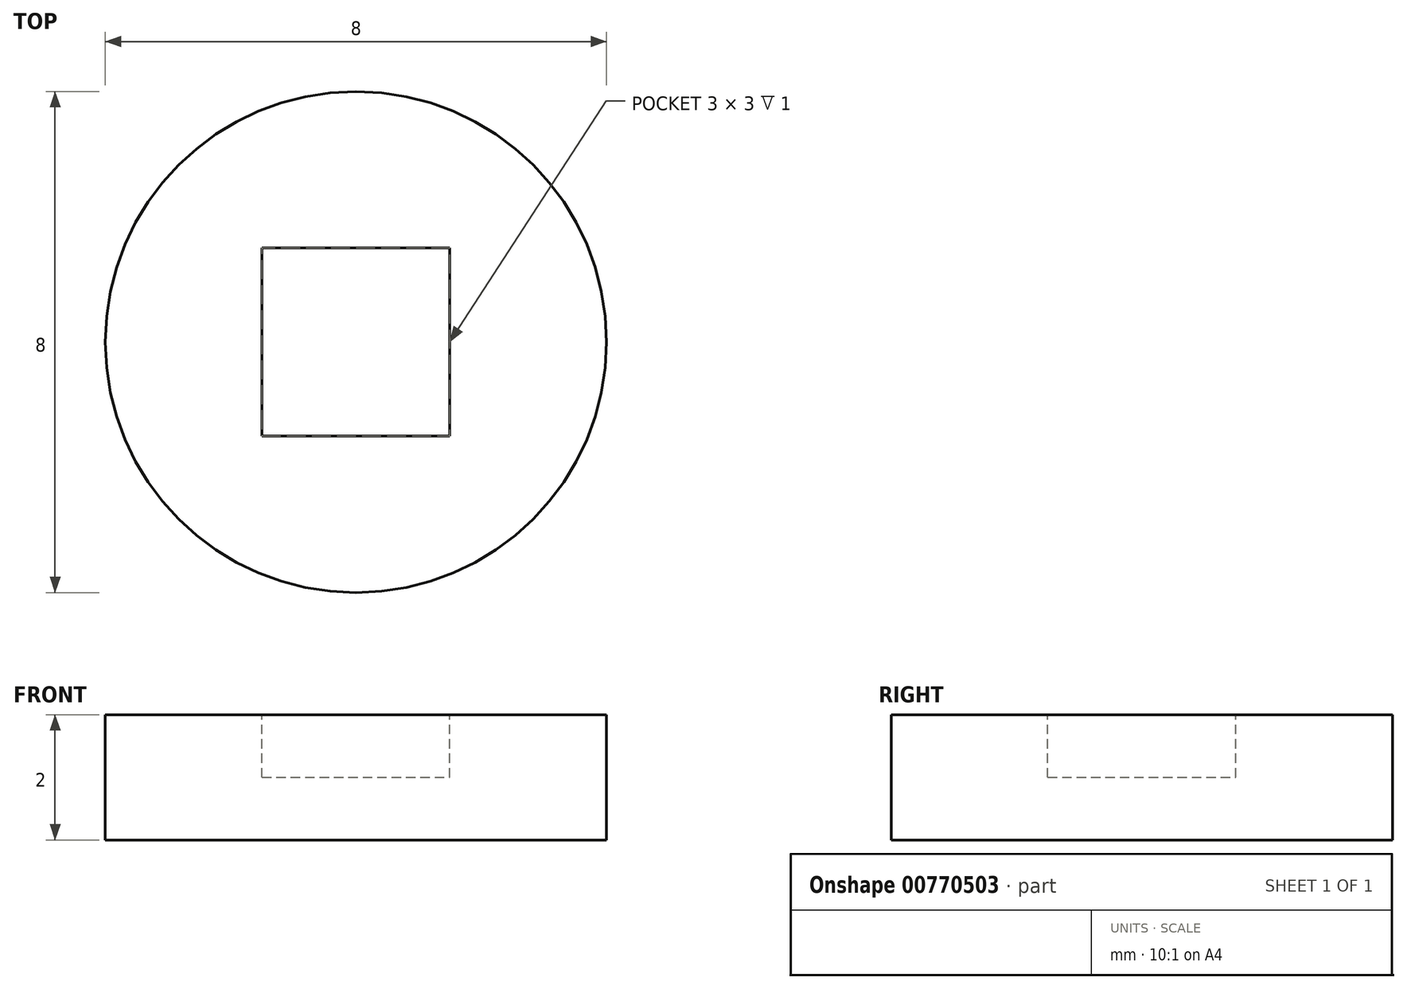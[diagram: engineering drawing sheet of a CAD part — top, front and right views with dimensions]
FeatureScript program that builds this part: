
annotation { "Feature Type Name" : "Feature", "Feature Type Description" : "" }
export const myFeature = defineFeature(function(context is Context, id is Id, definition is map)
    precondition{}
    {
        {
            var Q0;
            Q0=qCreatedBy(makeId("Top.planeOp"),FACE);
            var sketch = newSketch(context, id + "F0", { "sketchPlane" : qUnion([Q0])});
            skCircle(sketch, "E0", {"center": v(0, 0) * mm, "radius": 4 * mm});
            skSolve(sketch);
        }
        {
            var Q0;
            Q0=makeQuery(id+"F0.imprint","IMPRINT",FACE,{"disambiguationData":[TD([[makeQuery(id+"F0.imprint","IMPRINT",EDGE,{"derivedFrom":sQuery(id+"F0.wireOp",EDGE,"E0")}),1.0]])]});
            extrude(context, id + "F1", {"entities" : qUnion([Q0]), "oppositeDirection" : true, "depth" : 2 * mm, "offsetDistance" : 25 * mm});
        }
        {
            var Q0;
            Q0=makeQuery(id+"F1.opExtrude","CAP_FACE",FACE,{"disambiguationData":[OSD([sQuery(id+"F0.wireOp",EDGE,"E0")])],"isStart":true});
            var sketch = newSketch(context, id + "F2", { "sketchPlane" : qUnion([Q0])});
            skLineSegment(sketch, "E1.bottom", {"start": v(-1.5, -1.5) * mm, "end": v(1.5, -1.5) * mm});
            skLineSegment(sketch, "E1.top", {"start": v(-1.5, 1.5) * mm, "end": v(1.5, 1.5) * mm});
            skLineSegment(sketch, "E1.left", {"start": v(-1.5, -1.5) * mm, "end": v(-1.5, 1.5) * mm});
            skLineSegment(sketch, "E1.right", {"start": v(1.5, -1.5) * mm, "end": v(1.5, 1.5) * mm});
            skSolve(sketch);
        }
        {
            var Q0;
            Q0 = qSketchRegion(id + "F2", true);
            extrude(context, id + "F3", {"entities" : qUnion([Q0]), "operationType" : NewBodyOperationType.REMOVE, "oppositeDirection" : true, "depth" : 1 * mm, "offsetDistance" : 25 * mm});
        }
    });
